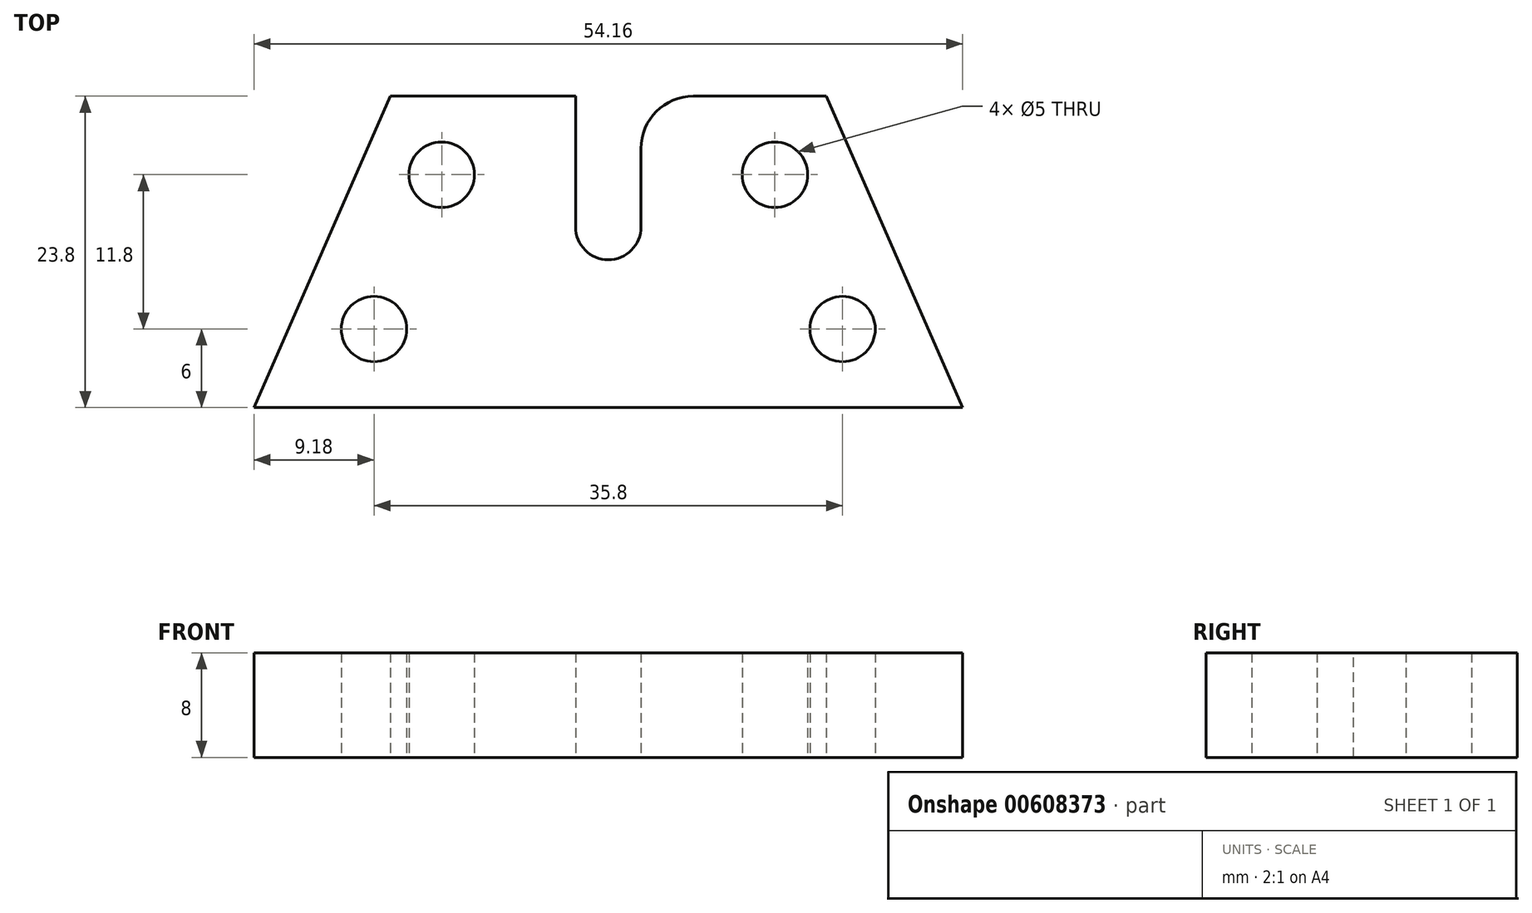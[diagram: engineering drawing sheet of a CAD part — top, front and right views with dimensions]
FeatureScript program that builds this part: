
annotation { "Feature Type Name" : "Feature", "Feature Type Description" : "" }
export const myFeature = defineFeature(function(context is Context, id is Id, definition is map)
    precondition{}
    {
        {
            var Q0;
            Q0=qCreatedBy(makeId("Top.planeOp"),FACE);
            var sketch = newSketch(context, id + "F0", { "sketchPlane" : qUnion([Q0])});
            skPoint(sketch, "E0", {"position": v(0, 0) * mm});
            skPoint(sketch, "E1", {"position": v(12.73, 0) * mm});
            skPoint(sketch, "E2", {"position": v(-12.73, 0) * mm});
            skPoint(sketch, "E3", {"position": v(0, -11.8) * mm});
            skPoint(sketch, "E4", {"position": v(-17.9, -11.8) * mm});
            skPoint(sketch, "E5", {"position": v(17.9, -11.8) * mm});
            skLineSegment(sketch, "E6", {"start": v(-12.73, 0) * mm, "end": v(-17.9, -11.8) * mm});
            skLineSegment(sketch, "E7", {"start": v(17.9, -11.8) * mm, "end": v(-17.9, -11.8) * mm});
            skLineSegment(sketch, "E8", {"start": v(17.9, -11.8) * mm, "end": v(12.73, 0) * mm});
            skLineSegment(sketch, "E9", {"start": v(12.73, 0) * mm, "end": v(-12.73, 0) * mm});
            skLineSegment(sketch, "E10.0", {"start": v(-16.65, 6) * mm, "end": v(-27.08, -17.8) * mm});
            skLineSegment(sketch, "E10.1", {"start": v(16.65, 6) * mm, "end": v(-16.65, 6) * mm});
            skLineSegment(sketch, "E10.2", {"start": v(27.08, -17.8) * mm, "end": v(16.65, 6) * mm});
            skLineSegment(sketch, "E10.3", {"start": v(27.08, -17.8) * mm, "end": v(-27.08, -17.8) * mm});
            skCircle(sketch, "E11", {"center": v(-12.73, 0) * mm, "radius": 2.5 * mm});
            skCircle(sketch, "E12", {"center": v(12.73, 0) * mm, "radius": 2.5 * mm});
            skCircle(sketch, "E13", {"center": v(-17.9, -11.8) * mm, "radius": 2.5 * mm});
            skCircle(sketch, "E14", {"center": v(17.9, -11.8) * mm, "radius": 2.5 * mm});
            skSolve(sketch);
        }
        {
            var Q0;
            Q0=makeQuery(id+"F0.imprint","IMPRINT",FACE,{"disambiguationData":[TD([[makeQuery(id+"F0.imprint","IMPRINT",EDGE,{"derivedFrom":sQuery(id+"F0.wireOp",EDGE,"E10.0")}),1.0]])]});
            var Q1;
            {var subQ3=sQuery(id+"F0.wireOp",EDGE,"E11");var subQ13=sQuery(id+"F0.wireOp",EDGE,"E6");var subQ14=makeQuery(id+"F0.imprint","INTERSECT",VERTEX,{"derivedFrom":[subQ13,subQ3]});Q1=makeQuery(id+"F0.imprint","IMPRINT",FACE,{"disambiguationData":[TD([[makeQuery(id+"F0.imprint","IMPRINT",EDGE,{"disambiguationData":[TD([[subQ14,-1.0]])],"derivedFrom":subQ13}),1.0]])]});}
            extrude(context, id + "F1", {"entities" : qUnion([Q0, Q1]), "depth" : 13 * mm, "offsetDistance" : 25 * mm});
        }
        {
            var Q0;
            Q0=makeQuery(id+"F1.opExtrude","SWEPT_FACE",FACE,{"disambiguationData":[OSD([sQuery(id+"F0.wireOp",EDGE,"E10.1")])]});
            var sketch = newSketch(context, id + "F2", { "sketchPlane" : qUnion([Q0])});
            skLineSegment(sketch, "E15.bottom", {"start": v(-2.5, 13) * mm, "end": v(2.5, 13) * mm});
            skLineSegment(sketch, "E15.top", {"start": v(-2.5, 0) * mm, "end": v(2.5, 0) * mm});
            skLineSegment(sketch, "E15.left", {"start": v(-2.5, 13) * mm, "end": v(-2.5, 0) * mm});
            skLineSegment(sketch, "E15.right", {"start": v(2.5, 13) * mm, "end": v(2.5, 0) * mm});
            skPoint(sketch, "E15.middle", {"position": v(0, 6.5) * mm});
            skPoint(sketch, "E15.middle.positionSnap0", {"position": v(16.65, 6.5) * mm});
            skPoint(sketch, "E15.centerSnap0", {"position": v(16.65, 6.5) * mm});
            skSolve(sketch);
        }
        {
            var Q0;
            Q0=makeQuery(id+"F2.imprint","IMPRINT",FACE,{"disambiguationData":[TD([[makeQuery(id+"F2.imprint","IMPRINT",EDGE,{"derivedFrom":sQuery(id+"F2.wireOp",EDGE,"E15.bottom")}),-1.0]])]});
            extrude(context, id + "F3", {"entities" : qUnion([Q0]), "operationType" : NewBodyOperationType.REMOVE, "oppositeDirection" : true, "depth" : 10 * mm, "offsetDistance" : 25 * mm});
        }
        {
            var Q0;
            Q0=makeQuery(id+"F1.opExtrude","CAP_FACE",FACE,{"disambiguationData":[OSD([sQuery(id+"F0.wireOp",EDGE,"E10.0"),sQuery(id+"F0.wireOp",EDGE,"E10.1"),sQuery(id+"F0.wireOp",EDGE,"E10.2"),sQuery(id+"F0.wireOp",EDGE,"E10.3"),sQuery(id+"F0.wireOp",EDGE,"E11"),sQuery(id+"F0.wireOp",EDGE,"E12"),sQuery(id+"F0.wireOp",EDGE,"E13"),sQuery(id+"F0.wireOp",EDGE,"E14")])],"isStart":false});
            var sketch = newSketch(context, id + "F4", { "sketchPlane" : qUnion([Q0])});
            skArc(sketch, "E16", {"start": v(-2.5, -4) * mm, "mid": v(0, -6.5) * mm, "end": v(2.5, -4) * mm});
            skPoint(sketch, "E17", {"position": v(-2.5, -4) * mm});
            skPoint(sketch, "E18", {"position": v(2.5, -4) * mm});
            skSolve(sketch);
        }
        {
            var Q0;
            Q0=makeQuery(id+"F4.imprint","IMPRINT",FACE,{"disambiguationData":[TD([[makeQuery(id+"F4.imprint","IMPRINT",EDGE,{"derivedFrom":sQuery(id+"F4.wireOp",EDGE,"E16")}),1.0]])]});
            extrude(context, id + "F5", {"entities" : qUnion([Q0]), "operationType" : NewBodyOperationType.REMOVE, "oppositeDirection" : true, "depth" : 25 * mm, "offsetDistance" : 25 * mm});
        }
        {
            var Q0;
            Q0=makeQuery(id+"F3.boolean.opBoolean","COPY",EDGE,{"derivedFrom":makeQuery(id+"F3.opExtrude","CAP_EDGE",EDGE,{"disambiguationData":[OSD([sQuery(id+"F2.wireOp",EDGE,"E15.left")])],"isStart":true})});
            var Q1;
            Q1=makeQuery(id+"F3.boolean.opBoolean","COPY",EDGE,{"derivedFrom":makeQuery(id+"F3.opExtrude","CAP_EDGE",EDGE,{"disambiguationData":[OSD([sQuery(id+"F2.wireOp",EDGE,"E15.right")])],"isStart":true})});
            fillet(context, id + "F6", {"entities" : qUnion([Q0, Q1]), "radius" : 4 * mm, "tangentPropagation" : true, "allowEdgeOverflow" : false});
        }
        {
            var Q0;
            Q0=makeQuery(id+"F1.opExtrude","CAP_FACE",FACE,{"disambiguationData":[OSD([sQuery(id+"F0.wireOp",EDGE,"E10.0"),sQuery(id+"F0.wireOp",EDGE,"E10.1"),sQuery(id+"F0.wireOp",EDGE,"E10.2"),sQuery(id+"F0.wireOp",EDGE,"E10.3"),sQuery(id+"F0.wireOp",EDGE,"E11"),sQuery(id+"F0.wireOp",EDGE,"E12"),sQuery(id+"F0.wireOp",EDGE,"E13"),sQuery(id+"F0.wireOp",EDGE,"E14")])],"isStart":false});
            extrude(context, id + "F7", {"entities" : qUnion([Q0]), "operationType" : NewBodyOperationType.REMOVE, "oppositeDirection" : true, "depth" : 5 * mm, "offsetDistance" : 25 * mm});
        }
    });
